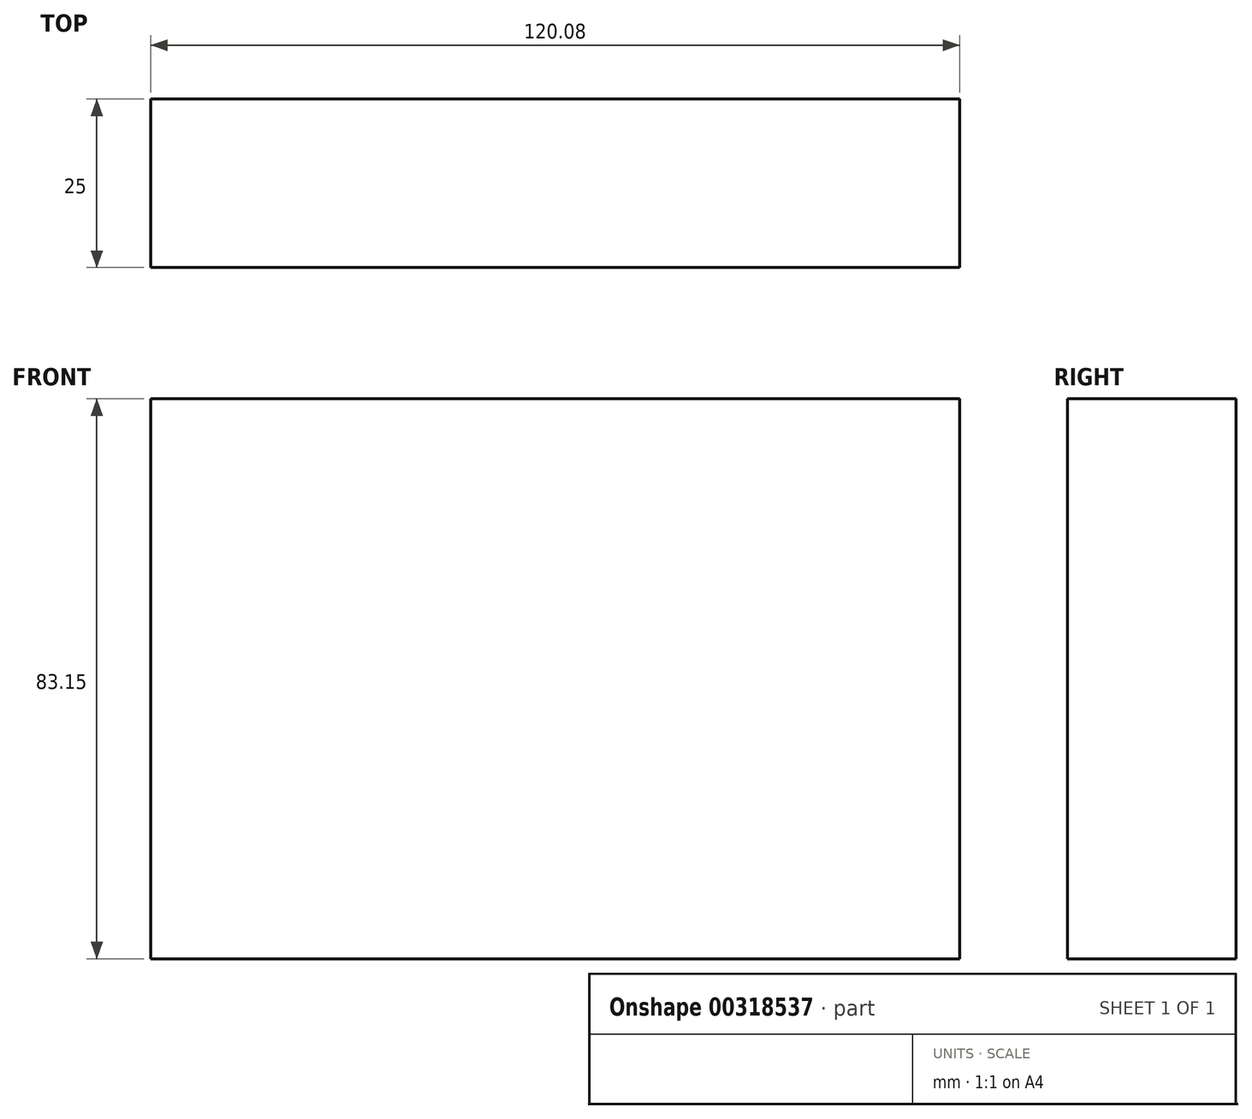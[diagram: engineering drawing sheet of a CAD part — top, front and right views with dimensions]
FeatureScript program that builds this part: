
annotation { "Feature Type Name" : "Feature", "Feature Type Description" : "" }
export const myFeature = defineFeature(function(context is Context, id is Id, definition is map)
    precondition{}
    {
        {
            var Q0;
            Q0=qCreatedBy(makeId("Front.planeOp"),FACE);
            var sketch = newSketch(context, id + "F0", { "sketchPlane" : qUnion([Q0])});
            skLineSegment(sketch, "E0.bottom", {"start": v(-43.65, 55.88) * mm, "end": v(76.43, 55.88) * mm});
            skLineSegment(sketch, "E0.top", {"start": v(-43.65, -27.27) * mm, "end": v(76.43, -27.27) * mm});
            skLineSegment(sketch, "E0.left", {"start": v(-43.65, 55.88) * mm, "end": v(-43.65, -27.27) * mm});
            skLineSegment(sketch, "E0.right", {"start": v(76.43, 55.88) * mm, "end": v(76.43, -27.27) * mm});
            skSolve(sketch);
        }
        {
            var Q0;
            Q0 = qSketchRegion(id + "F0", true);
            extrude(context, id + "F1", {"entities" : qUnion([Q0]), "depth" : 25 * mm});
        }
    });
